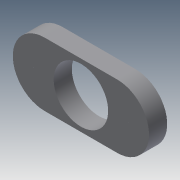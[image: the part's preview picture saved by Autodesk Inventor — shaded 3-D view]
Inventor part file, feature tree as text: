
AUTODESK INVENTOR PART (.ipt)
format: ipt  version: 2013 (Build 170138000, 138)  size: 96,768 bytes
history: native  units: mm
features: extrude x2, sketch x2
ambient origin geometry x8: Origin, YZ Plane, XZ Plane, XY Plane, X Axis, Y Axis, Z Axis, Center Point
bodies: Solid1 (feature_tree)
feature tree (4):
  extrude  "Extrusion1"  Depth=35.0mm
  extrude  "Extrusion2"  Depth=10.0mm TaperAngle=0.0deg
  sketch  "Sketch1"  dims[d0=40.0mm d1=35.0mm]
  sketch  "Sketch2"  dims[d2=30.0mm d3=10.0mm d4=0.0mm d5=0.2mm d6=0.2mm d7=10.0mm d8=0.0mm]
